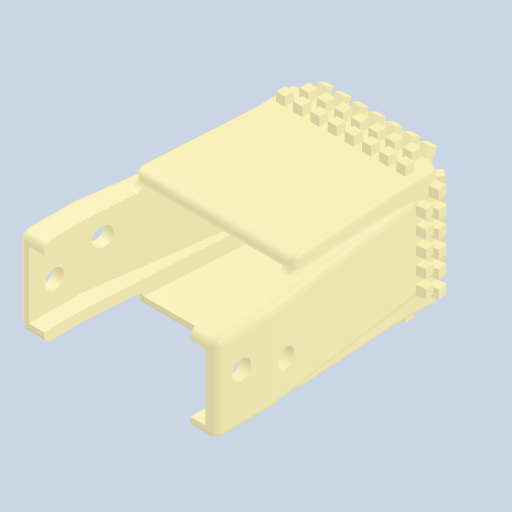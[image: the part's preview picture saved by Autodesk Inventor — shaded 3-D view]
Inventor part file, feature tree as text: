
AUTODESK INVENTOR PART (.ipt)
format: ipt  version: 2023 (Build 270158000, 158)  size: 1,447,424 bytes
history: native  units: mm
features: other x28, extrude x18, fillet x4, mirror x2, loft x1, pattern_circular x1
ambient origin geometry x8: Origin, YZ Plane, XZ Plane, XY Plane, X Axis, Y Axis, Z Axis, Center Point
bodies: Solid1 (feature_tree)
feature tree (54):
  other  "NP1_Payload.ipt"
  other  "Sk:Params"
  extrude  "Ex:FrontSide"  Depth=10.0mm
  extrude  "Ex:FrontLip"  Depth=2.2mm
  other  "EndPlane"
  other  "SidePlane1"
  other  "Sk:EndCone"
  other  "Sk:MiddleLift"
  extrude  "Ex:MiddleLift"  TaperAngle=0.0deg  [1 undecoded]
  extrude  "Ex:FrontLift"  Depth=0.7mm
  loft  "Loft:EndCone"
  other  "FrontPlane"
  other  "SidePlane2"
  fillet  "Fillet:CircularEnd"  Radius=0.8mm
  other  "AnglePlane1"
  other  "Sk:AngleNub1"
  extrude  "Ex:AngleNub1-1"  TaperAngle=0.0deg  [1 undecoded]
  extrude  "Ex:AngleNub1-2"  Depth=0.2mm
  extrude  "Ex:AngleNub1-3"  TaperAngle=0.0deg  [1 undecoded]
  extrude  "Ex:AngleNub1-4"  Depth=0.7mm
  other  "AnglePlane2"
  other  "Sk:AngleNub2"
  extrude  "Ex:AngleNub2-1"  Depth=0.7mm
  extrude  "Ex:AngleNub2-2"  Depth=5.0mm
  extrude  "Ex:AngleNub2-3"  Depth=0.2mm
  extrude  "Ex:AngleNub2-4"  Depth=0.25mm
  extrude  "Ex:SideNub1"  Depth=0.1mm
  other  "Sk:SideNub2"
  extrude  "Ex:SideNub2"  Depth=0.7mm
  fillet  "Fillet:Touchup"  Radius=3.5mm
  mirror  "Mirror1"
  mirror  "Mirror2"
  other  "SidePlane3"
  extrude  "Ex:UpperHole"  Depth=0.2mm
  extrude  "Ex:LowerHole"  Depth=0.7mm
  pattern_circular  "Pat:ReverseHoles"  [2 undecoded]
  fillet  "Fillet:FinalThin"  Radius=0.2mm
  fillet  "Fillet:FinalThick"  Radius=20.0mm
  other  "Sk:EndPlaneProj"
  other  "SlicePlane1"
  other  "SlicePlane2"
  extrude  "Ex:Slice1"  TaperAngle=360.0deg  [1 undecoded]
  extrude  "Ex:Slice2"  Depth=1.25mm
  other  "TaggingFeature1"
  other  "Sk: Base"
  other  "Sk:FrontLip"
  other  "Sk:UpperHole"
  other  "Sk:LowerHole"
  other  "Sk:SideNub1"
  other  "Edges4"
  other  "Sk:Slice1"
  other  "Sk:Slice2"
  other  "Solid1::NP1_Payload.ipt"
  other  "Srf1"
note: 6 required parameter values undecoded (feature->parameter linkage not recoverable at this tier; creation-order binding heuristic only, values carry confidence <= 0.55)
